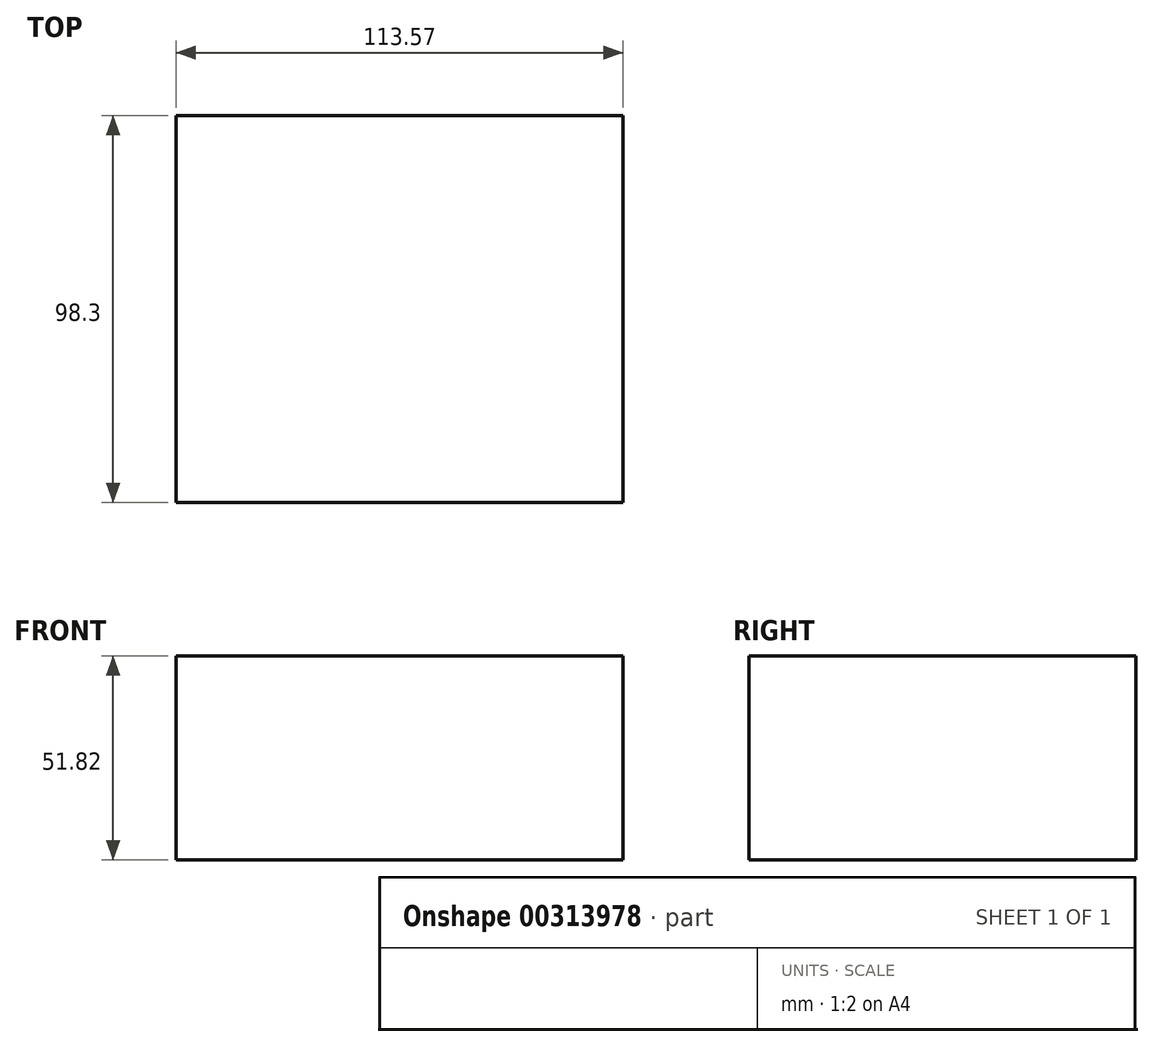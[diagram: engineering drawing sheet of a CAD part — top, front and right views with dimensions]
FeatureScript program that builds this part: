
annotation { "Feature Type Name" : "Feature", "Feature Type Description" : "" }
export const myFeature = defineFeature(function(context is Context, id is Id, definition is map)
    precondition{}
    {
        {
            var Q0;
            Q0=qCreatedBy(makeId("Front.planeOp"),FACE);
            var sketch = newSketch(context, id + "F0", { "sketchPlane" : qUnion([Q0])});
            skLineSegment(sketch, "E0.bottom", {"start": v(-55.33, 8.57) * mm, "end": v(58.24, 8.57) * mm});
            skLineSegment(sketch, "E0.top", {"start": v(-55.33, -66.82) * mm, "end": v(58.24, -66.82) * mm});
            skLineSegment(sketch, "E0.left", {"start": v(-55.33, 8.57) * mm, "end": v(-55.33, -66.82) * mm});
            skLineSegment(sketch, "E0.right", {"start": v(58.24, 8.57) * mm, "end": v(58.24, -66.82) * mm});
            skSolve(sketch);
        }
        {
            var Q0;
            Q0=sQuery(id+"F0.wireOp",EDGE,"E0.top");
            extrude(context, id + "F1", {"bodyType" : ToolBodyType.SURFACE, "surfaceEntities" : qUnion([Q0]), "depth" : 98.3 * mm});
        }
        {
            var Q0;
            Q0=makeQuery(id+"F1.opExtrude","SWEPT_FACE",FACE,{"disambiguationData":[OSD([sQuery(id+"F0.wireOp",EDGE,"E0.top")])]});
            extrude(context, id + "F2", {"entities" : qUnion([Q0]), "oppositeDirection" : true, "depth" : 51.82 * mm});
        }
    });
